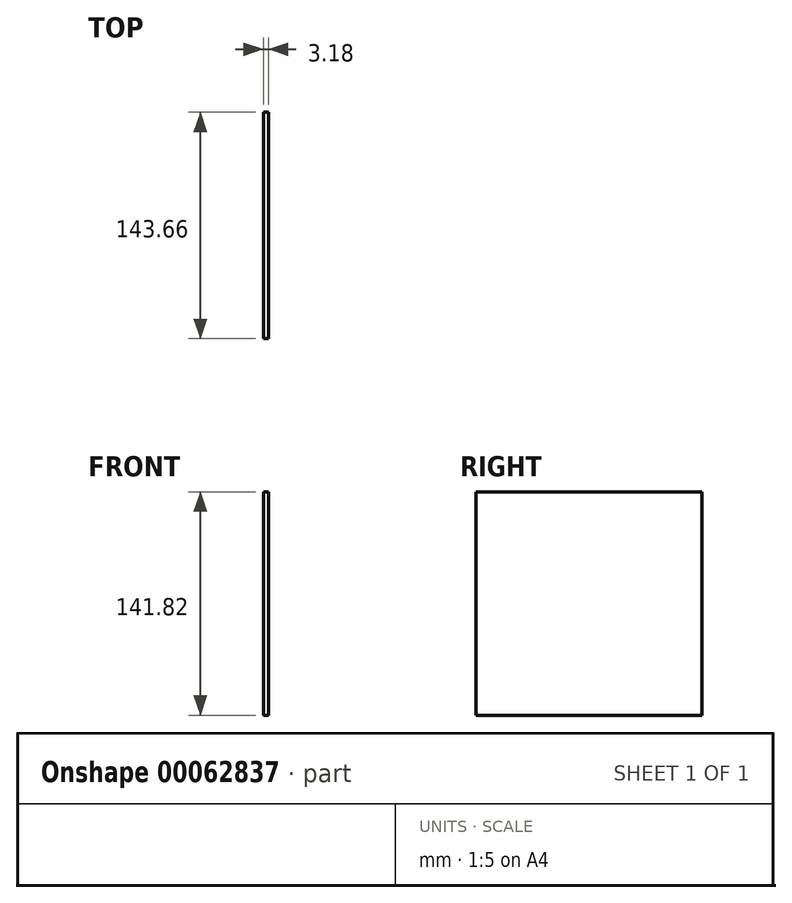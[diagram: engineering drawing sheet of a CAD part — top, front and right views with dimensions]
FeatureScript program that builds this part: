
annotation { "Feature Type Name" : "Feature", "Feature Type Description" : "" }
export const myFeature = defineFeature(function(context is Context, id is Id, definition is map)
    precondition{}
    {
        {
            var Q0;
            Q0=qCreatedBy(makeId("Right.planeOp"),FACE);
            var sketch = newSketch(context, id + "F0", { "sketchPlane" : qUnion([Q0])});
            skLineSegment(sketch, "E0.rect.bottom", {"start": v(-71.82, 70.91) * mm, "end": v(71.83, 70.91) * mm});
            skLineSegment(sketch, "E0.rect.top", {"start": v(-71.83, -70.91) * mm, "end": v(71.82, -70.91) * mm});
            skLineSegment(sketch, "E0.rect.left", {"start": v(-71.82, 70.91) * mm, "end": v(-71.83, -70.91) * mm});
            skLineSegment(sketch, "E0.rect.right", {"start": v(71.83, 70.91) * mm, "end": v(71.82, -70.91) * mm});
            skPoint(sketch, "E0.rect.middle", {"position": v(0, 0) * mm});
            skSolve(sketch);
        }
        {
            var Q0;
            Q0=makeQuery(id+"F0.imprint","IMPRINT",FACE,{"disambiguationData":[TD([[makeQuery(id+"F0.imprint","IMPRINT",EDGE,{"derivedFrom":sQuery(id+"F0.wireOp",EDGE,"E0.rect.bottom")}),-1.0]])]});
            extrude(context, id + "F1", {"entities" : qUnion([Q0]), "endBound" : BoundingType.SYMMETRIC, "depth" : 3.17 * mm});
        }
    });
